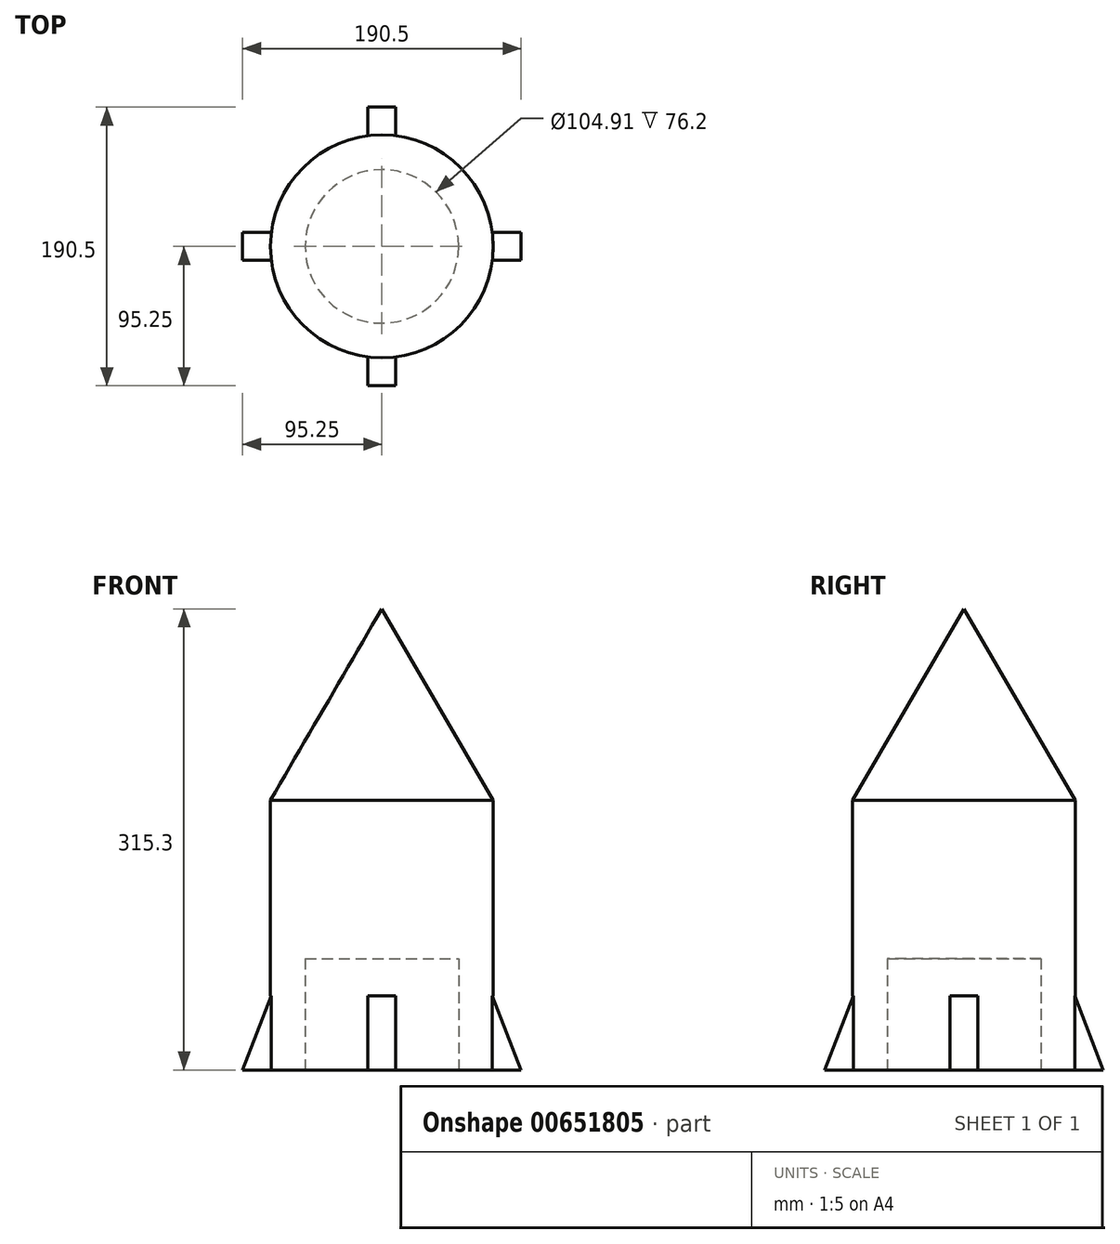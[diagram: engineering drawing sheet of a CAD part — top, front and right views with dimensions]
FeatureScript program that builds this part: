
annotation { "Feature Type Name" : "Feature", "Feature Type Description" : "" }
export const myFeature = defineFeature(function(context is Context, id is Id, definition is map)
    precondition{}
    {
        {
            var Q0;
            Q0=qCreatedBy(makeId("Right.planeOp"),FACE);
            var sketch = newSketch(context, id + "F0", { "sketchPlane" : qUnion([Q0])});
            skLineSegment(sketch, "E0.bottom", {"start": v(0, -92.22) * mm, "end": v(-76.2, -92.22) * mm});
            skLineSegment(sketch, "E0.top", {"start": v(0, 92.22) * mm, "end": v(-76.2, 92.22) * mm});
            skLineSegment(sketch, "E0.right", {"start": v(-76.2, -92.22) * mm, "end": v(-76.2, 92.22) * mm});
            skPoint(sketch, "E0.middle", {"position": v(0, 0) * mm});
            skLineSegment(sketch, "E1", {"start": v(0, 92.22) * mm, "end": v(0, 223.08) * mm});
            skLineSegment(sketch, "E2", {"start": v(0, 223.08) * mm, "end": v(-76.2, 92.22) * mm});
            skLineSegment(sketch, "E3", {"start": v(0, 92.22) * mm, "end": v(0, -92.22) * mm});
            skPoint(sketch, "E0.left.start.orphan", {"position": v(76.2, -92.22) * mm});
            skPoint(sketch, "E4.orphan", {"position": v(76.2, 92.22) * mm});
            skSolve(sketch);
        }
        {
            var Q0;
            Q0=makeQuery(id+"F0.imprint","IMPRINT",FACE,{"disambiguationData":[TD([[makeQuery(id+"F0.imprint","IMPRINT",EDGE,{"derivedFrom":sQuery(id+"F0.wireOp",EDGE,"E0.top")}),-1.0]])]});
            var Q1;
            Q1=makeQuery(id+"F0.imprint","IMPRINT",FACE,{"disambiguationData":[TD([[makeQuery(id+"F0.imprint","IMPRINT",EDGE,{"derivedFrom":sQuery(id+"F0.wireOp",EDGE,"E0.bottom")}),-1.0]])]});
            var Q2;
            Q2=sQuery(id+"F0.wireOp",EDGE,"E3");
            revolve(context, id + "F1", {"entities" : qUnion([Q0, Q1]), "axis" : qUnion([Q2]), "revolveType" : RevolveType.FULL});
        }
        {
            var Q0;
            Q0=makeQuery(id+"F1.opRevolve","SWEPT_FACE",FACE,{"disambiguationData":[OSD([sQuery(id+"F0.wireOp",EDGE,"E0.bottom")])]});
            var sketch = newSketch(context, id + "F2", { "sketchPlane" : qUnion([Q0])});
            skCircle(sketch, "E5", {"center": v(0, 0) * mm, "radius": 52.45 * mm});
            skSolve(sketch);
        }
        {
            var Q0;
            Q0=makeQuery(id+"F2.imprint","IMPRINT",FACE,{"disambiguationData":[TD([[makeQuery(id+"F2.imprint","IMPRINT",EDGE,{"derivedFrom":sQuery(id+"F2.wireOp",EDGE,"E5")}),1.0]])]});
            extrude(context, id + "F3", {"entities" : qUnion([Q0]), "operationType" : NewBodyOperationType.REMOVE, "oppositeDirection" : true, "depth" : 76.2 * mm, "offsetDistance" : 25.4 * mm});
        }
        {
            var Q0;
            Q0=makeQuery(id+"F1.opRevolve","SWEPT_FACE",FACE,{"disambiguationData":[OSD([sQuery(id+"F0.wireOp",EDGE,"E0.bottom")])]});
            var sketch = newSketch(context, id + "F4", { "sketchPlane" : qUnion([Q0])});
            skLineSegment(sketch, "E6", {"start": v(0, 0) * mm, "end": v(161.16, 0) * mm});
            skLineSegment(sketch, "E7", {"start": v(161.16, 0) * mm, "end": v(-168.42, 0) * mm});
            skLineSegment(sketch, "E8", {"start": v(-168.42, 0) * mm, "end": v(0, 0) * mm});
            skLineSegment(sketch, "E9", {"start": v(0, 107.36) * mm, "end": v(0, -91.11) * mm});
            skLineSegment(sketch, "E10.bottom", {"start": v(9.53, 57.15) * mm, "end": v(-9.52, 57.15) * mm});
            skLineSegment(sketch, "E10.top", {"start": v(9.53, 95.25) * mm, "end": v(-9.52, 95.25) * mm});
            skLineSegment(sketch, "E10.left", {"start": v(9.53, 57.15) * mm, "end": v(9.53, 95.25) * mm});
            skLineSegment(sketch, "E10.right", {"start": v(-9.52, 57.15) * mm, "end": v(-9.52, 95.25) * mm});
            skPoint(sketch, "E10.middle", {"position": v(0, 76.2) * mm});
            skLineSegment(sketch, "E11.bottom", {"start": v(-95.25, 9.52) * mm, "end": v(-57.15, 9.52) * mm});
            skLineSegment(sketch, "E11.top", {"start": v(-95.25, -9.52) * mm, "end": v(-57.15, -9.52) * mm});
            skLineSegment(sketch, "E11.left", {"start": v(-95.25, 9.52) * mm, "end": v(-95.25, -9.53) * mm});
            skLineSegment(sketch, "E11.right", {"start": v(-57.15, 9.52) * mm, "end": v(-57.15, -9.53) * mm});
            skPoint(sketch, "E11.middle", {"position": v(-76.2, 0) * mm});
            skLineSegment(sketch, "E12.bottom", {"start": v(95.25, -9.53) * mm, "end": v(57.15, -9.53) * mm});
            skLineSegment(sketch, "E12.top", {"start": v(95.25, 9.52) * mm, "end": v(57.15, 9.52) * mm});
            skLineSegment(sketch, "E12.left", {"start": v(95.25, -9.53) * mm, "end": v(95.25, 9.53) * mm});
            skLineSegment(sketch, "E12.right", {"start": v(57.15, -9.53) * mm, "end": v(57.15, 9.53) * mm});
            skPoint(sketch, "E12.middle", {"position": v(76.2, 0) * mm});
            skPoint(sketch, "E12.middle.positionSnap0", {"position": v(80.58, 0) * mm});
            skPoint(sketch, "E12.centerSnap0", {"position": v(80.58, 0) * mm});
            skLineSegment(sketch, "E13.bottom", {"start": v(9.53, -95.25) * mm, "end": v(-9.52, -95.25) * mm});
            skLineSegment(sketch, "E13.top", {"start": v(9.53, -57.15) * mm, "end": v(-9.52, -57.15) * mm});
            skLineSegment(sketch, "E13.left", {"start": v(9.53, -95.25) * mm, "end": v(9.53, -57.15) * mm});
            skLineSegment(sketch, "E13.right", {"start": v(-9.52, -95.25) * mm, "end": v(-9.52, -57.15) * mm});
            skPoint(sketch, "E13.middle", {"position": v(0, -76.2) * mm});
            skSolve(sketch);
        }
        {
            var Q0;
            {var subQ0=sQuery(id+"F4.wireOp",EDGE,"E12.left");var subQ5=sQuery(id+"F4.wireOp",EDGE,"E12.bottom");var subQ6=makeQuery(id+"F4.imprint","INTERSECT",VERTEX,{"derivedFrom":[subQ5,subQ0]});Q0=makeQuery(id+"F4.imprint","IMPRINT",FACE,{"disambiguationData":[TD([[makeQuery(id+"F4.imprint","IMPRINT",EDGE,{"disambiguationData":[TD([[subQ6,-1.0]])],"derivedFrom":subQ0}),1.0]])]});}
            var Q1;
            {var subQ0=sQuery(id+"F4.wireOp",EDGE,"E12.left");var subQ5=sQuery(id+"F4.wireOp",EDGE,"E12.top");var subQ6=makeQuery(id+"F4.imprint","INTERSECT",VERTEX,{"derivedFrom":[subQ5,subQ0]});Q1=makeQuery(id+"F4.imprint","IMPRINT",FACE,{"disambiguationData":[TD([[makeQuery(id+"F4.imprint","IMPRINT",EDGE,{"disambiguationData":[TD([[subQ6,1.0]])],"derivedFrom":subQ0}),1.0]])]});}
            var Q2;
            {var subQ0=sQuery(id+"F4.wireOp",EDGE,"E11.left");var subQ5=sQuery(id+"F4.wireOp",EDGE,"E11.top");var subQ6=makeQuery(id+"F4.imprint","INTERSECT",VERTEX,{"derivedFrom":[subQ5,subQ0]});Q2=makeQuery(id+"F4.imprint","IMPRINT",FACE,{"disambiguationData":[TD([[makeQuery(id+"F4.imprint","IMPRINT",EDGE,{"disambiguationData":[TD([[subQ6,1.0]])],"derivedFrom":subQ0}),1.0]])]});}
            var Q3;
            {var subQ0=sQuery(id+"F4.wireOp",EDGE,"E10.top");var subQ5=sQuery(id+"F4.wireOp",EDGE,"E10.left");var subQ6=makeQuery(id+"F4.imprint","INTERSECT",VERTEX,{"derivedFrom":[subQ0,subQ5]});Q3=makeQuery(id+"F4.imprint","IMPRINT",FACE,{"disambiguationData":[TD([[makeQuery(id+"F4.imprint","IMPRINT",EDGE,{"disambiguationData":[TD([[subQ6,-1.0]])],"derivedFrom":subQ0}),1.0]])]});}
            var Q4;
            {var subQ0=sQuery(id+"F4.wireOp",EDGE,"E10.top");var subQ5=sQuery(id+"F4.wireOp",EDGE,"E10.right");var subQ6=makeQuery(id+"F4.imprint","INTERSECT",VERTEX,{"derivedFrom":[subQ0,subQ5]});Q4=makeQuery(id+"F4.imprint","IMPRINT",FACE,{"disambiguationData":[TD([[makeQuery(id+"F4.imprint","IMPRINT",EDGE,{"disambiguationData":[TD([[subQ6,1.0]])],"derivedFrom":subQ0}),1.0]])]});}
            var Q5;
            {var subQ0=sQuery(id+"F4.wireOp",EDGE,"E12.right");var subQ5=sQuery(id+"F4.wireOp",EDGE,"E12.bottom");var subQ7=makeQuery(id+"F4.imprint","INTERSECT",VERTEX,{"derivedFrom":[subQ5,subQ0]});Q5=makeQuery(id+"F4.imprint","IMPRINT",FACE,{"disambiguationData":[TD([[makeQuery(id+"F4.imprint","IMPRINT",EDGE,{"disambiguationData":[TD([[subQ7,-1.0]])],"derivedFrom":subQ0}),-1.0]])]});}
            var Q6;
            {var subQ0=sQuery(id+"F4.wireOp",EDGE,"E12.right");var subQ5=sQuery(id+"F4.wireOp",EDGE,"E12.top");var subQ6=makeQuery(id+"F4.imprint","INTERSECT",VERTEX,{"derivedFrom":[subQ5,subQ0]});Q6=makeQuery(id+"F4.imprint","IMPRINT",FACE,{"disambiguationData":[TD([[makeQuery(id+"F4.imprint","IMPRINT",EDGE,{"disambiguationData":[TD([[subQ6,1.0]])],"derivedFrom":subQ0}),-1.0]])]});}
            var Q7;
            {var subQ0=sQuery(id+"F4.wireOp",EDGE,"E11.right");var subQ5=sQuery(id+"F4.wireOp",EDGE,"E11.bottom");var subQ6=makeQuery(id+"F4.imprint","INTERSECT",VERTEX,{"derivedFrom":[subQ5,subQ0]});Q7=makeQuery(id+"F4.imprint","IMPRINT",FACE,{"disambiguationData":[TD([[makeQuery(id+"F4.imprint","IMPRINT",EDGE,{"disambiguationData":[TD([[subQ6,-1.0]])],"derivedFrom":subQ0}),-1.0]])]});}
            var Q8;
            {var subQ0=sQuery(id+"F4.wireOp",EDGE,"E11.right");var subQ5=sQuery(id+"F4.wireOp",EDGE,"E11.top");var subQ6=makeQuery(id+"F4.imprint","INTERSECT",VERTEX,{"derivedFrom":[subQ5,subQ0]});Q8=makeQuery(id+"F4.imprint","IMPRINT",FACE,{"disambiguationData":[TD([[makeQuery(id+"F4.imprint","IMPRINT",EDGE,{"disambiguationData":[TD([[subQ6,1.0]])],"derivedFrom":subQ0}),-1.0]])]});}
            var Q9;
            {var subQ0=sQuery(id+"F4.wireOp",EDGE,"E10.bottom");var subQ5=sQuery(id+"F4.wireOp",EDGE,"E10.left");var subQ6=makeQuery(id+"F4.imprint","INTERSECT",VERTEX,{"derivedFrom":[subQ0,subQ5]});Q9=makeQuery(id+"F4.imprint","IMPRINT",FACE,{"disambiguationData":[TD([[makeQuery(id+"F4.imprint","IMPRINT",EDGE,{"disambiguationData":[TD([[subQ6,-1.0]])],"derivedFrom":subQ0}),-1.0]])]});}
            var Q10;
            {var subQ0=sQuery(id+"F4.wireOp",EDGE,"E10.bottom");var subQ5=sQuery(id+"F4.wireOp",EDGE,"E10.right");var subQ6=makeQuery(id+"F4.imprint","INTERSECT",VERTEX,{"derivedFrom":[subQ0,subQ5]});Q10=makeQuery(id+"F4.imprint","IMPRINT",FACE,{"disambiguationData":[TD([[makeQuery(id+"F4.imprint","IMPRINT",EDGE,{"disambiguationData":[TD([[subQ6,1.0]])],"derivedFrom":subQ0}),-1.0]])]});}
            var Q11;
            {var subQ0=sQuery(id+"F4.wireOp",EDGE,"E13.top");var subQ5=sQuery(id+"F4.wireOp",EDGE,"E13.left");var subQ6=makeQuery(id+"F4.imprint","INTERSECT",VERTEX,{"derivedFrom":[subQ0,subQ5]});Q11=makeQuery(id+"F4.imprint","IMPRINT",FACE,{"disambiguationData":[TD([[makeQuery(id+"F4.imprint","IMPRINT",EDGE,{"disambiguationData":[TD([[subQ6,-1.0]])],"derivedFrom":subQ0}),1.0]])]});}
            var Q12;
            {var subQ0=sQuery(id+"F4.wireOp",EDGE,"E13.top");var subQ5=sQuery(id+"F4.wireOp",EDGE,"E13.right");var subQ6=makeQuery(id+"F4.imprint","INTERSECT",VERTEX,{"derivedFrom":[subQ0,subQ5]});Q12=makeQuery(id+"F4.imprint","IMPRINT",FACE,{"disambiguationData":[TD([[makeQuery(id+"F4.imprint","IMPRINT",EDGE,{"disambiguationData":[TD([[subQ6,1.0]])],"derivedFrom":subQ0}),1.0]])]});}
            var Q13;
            {var subQ4=sQuery(id+"F4.wireOp",EDGE,"E13.bottom");Q13=makeQuery(id+"F4.imprint","IMPRINT",FACE,{"disambiguationData":[TD([[makeQuery(id+"F4.imprint","IMPRINT",EDGE,{"derivedFrom":subQ4}),-1.0]])]});}
            var Q14;
            {var subQ0=sQuery(id+"F4.wireOp",EDGE,"E11.left");var subQ5=sQuery(id+"F4.wireOp",EDGE,"E11.bottom");var subQ7=makeQuery(id+"F4.imprint","INTERSECT",VERTEX,{"derivedFrom":[subQ5,subQ0]});Q14=makeQuery(id+"F4.imprint","IMPRINT",FACE,{"disambiguationData":[TD([[makeQuery(id+"F4.imprint","IMPRINT",EDGE,{"disambiguationData":[TD([[subQ7,-1.0]])],"derivedFrom":subQ0}),1.0]])]});}
            extrude(context, id + "F5", {"entities" : qUnion([Q0, Q1, Q2, Q3, Q4, Q5, Q6, Q7, Q8, Q9, Q10, Q11, Q12, Q13, Q14]), "operationType" : NewBodyOperationType.ADD, "oppositeDirection" : true, "depth" : 50.8 * mm, "offsetDistance" : 25.4 * mm});
        }
        {
            var Q0;
            Q0=makeQuery(id+"F5.opExtrude","SWEPT_FACE",FACE,{"disambiguationData":[OSD([sQuery(id+"F4.wireOp",EDGE,"E12.bottom")])]});
            var sketch = newSketch(context, id + "F6", { "sketchPlane" : qUnion([Q0])});
            skLineSegment(sketch, "E14", {"start": v(-95.25, -92.22) * mm, "end": v(-75.6, -41.42) * mm});
            skLineSegment(sketch, "E15", {"start": v(-95.25, -92.22) * mm, "end": v(-95.25, -41.42) * mm});
            skLineSegment(sketch, "E16", {"start": v(-95.25, -41.42) * mm, "end": v(-75.6, -41.42) * mm});
            skSolve(sketch);
        }
        {
            var Q0;
            Q0 = qSketchRegion(id + "F6", true);
            extrude(context, id + "F7", {"entities" : qUnion([Q0]), "operationType" : NewBodyOperationType.REMOVE, "endBound" : BoundingType.THROUGH_ALL, "oppositeDirection" : true, "depth" : 25.4 * mm, "offsetDistance" : 25.4 * mm});
        }
        {
            var Q0;
            Q0=makeQuery(id+"F5.opExtrude","SWEPT_FACE",FACE,{"disambiguationData":[OSD([sQuery(id+"F4.wireOp",EDGE,"E10.left")])]});
            var sketch = newSketch(context, id + "F8", { "sketchPlane" : qUnion([Q0])});
            skLineSegment(sketch, "E17", {"start": v(-95.25, -92.22) * mm, "end": v(-75.6, -41.42) * mm});
            skLineSegment(sketch, "E18", {"start": v(-95.25, -92.22) * mm, "end": v(-95.25, -41.42) * mm});
            skLineSegment(sketch, "E19", {"start": v(-95.25, -41.42) * mm, "end": v(-85.43, -41.42) * mm});
            skSolve(sketch);
        }
        {
            var Q0;
            {var subQ0=sQuery(id+"F8.wireOp",EDGE,"E17");Q0=makeQuery(id+"F8.imprint","IMPRINT",FACE,{"disambiguationData":[TD([[makeQuery(id+"F8.imprint","IMPRINT",EDGE,{"derivedFrom":subQ0}),1.0]])]});}
            extrude(context, id + "F9", {"entities" : qUnion([Q0]), "operationType" : NewBodyOperationType.REMOVE, "endBound" : BoundingType.THROUGH_ALL, "oppositeDirection" : true, "depth" : 25.4 * mm, "offsetDistance" : 25.4 * mm});
        }
        {
            var Q0;
            Q0=makeQuery(id+"F5.opExtrude","SWEPT_FACE",FACE,{"disambiguationData":[OSD([sQuery(id+"F4.wireOp",EDGE,"E13.right")])]});
            var sketch = newSketch(context, id + "F10", { "sketchPlane" : qUnion([Q0])});
            skLineSegment(sketch, "E20", {"start": v(-95.25, -92.22) * mm, "end": v(-75.6, -41.42) * mm});
            skLineSegment(sketch, "E21", {"start": v(-95.25, -92.22) * mm, "end": v(-95.25, -41.42) * mm});
            skLineSegment(sketch, "E22", {"start": v(-95.25, -41.42) * mm, "end": v(-75.6, -41.42) * mm});
            skSolve(sketch);
        }
        {
            var Q0;
            Q0 = qSketchRegion(id + "F10", true);
            extrude(context, id + "F11", {"entities" : qUnion([Q0]), "operationType" : NewBodyOperationType.REMOVE, "endBound" : BoundingType.THROUGH_ALL, "oppositeDirection" : true, "depth" : 25.4 * mm, "offsetDistance" : 25.4 * mm});
        }
        {
            var Q0;
            Q0=makeQuery(id+"F5.opExtrude","SWEPT_FACE",FACE,{"disambiguationData":[OSD([sQuery(id+"F4.wireOp",EDGE,"E11.bottom")])]});
            var sketch = newSketch(context, id + "F12", { "sketchPlane" : qUnion([Q0])});
            skLineSegment(sketch, "E23", {"start": v(-95.25, -92.22) * mm, "end": v(-75.6, -41.42) * mm});
            skLineSegment(sketch, "E24", {"start": v(-95.25, -92.22) * mm, "end": v(-95.25, -41.42) * mm});
            skLineSegment(sketch, "E25", {"start": v(-95.25, -41.42) * mm, "end": v(-75.6, -41.42) * mm});
            skSolve(sketch);
        }
        {
            var Q0;
            Q0 = qSketchRegion(id + "F12", true);
            extrude(context, id + "F13", {"entities" : qUnion([Q0]), "operationType" : NewBodyOperationType.REMOVE, "endBound" : BoundingType.THROUGH_ALL, "oppositeDirection" : true, "depth" : 25.4 * mm, "offsetDistance" : 25.4 * mm});
        }
    });
